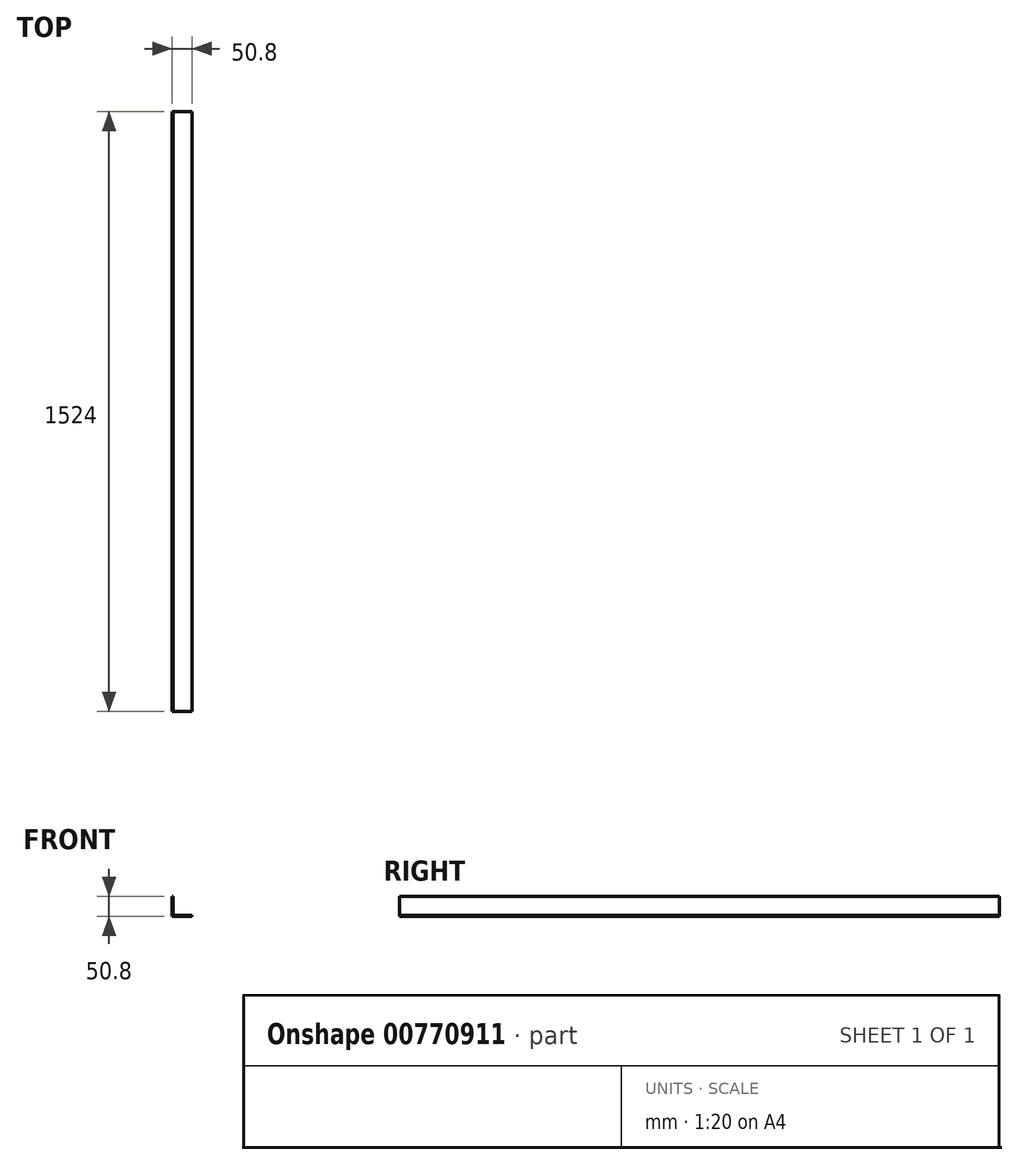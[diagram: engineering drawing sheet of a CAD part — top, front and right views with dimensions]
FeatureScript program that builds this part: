
annotation { "Feature Type Name" : "Feature", "Feature Type Description" : "" }
export const myFeature = defineFeature(function(context is Context, id is Id, definition is map)
    precondition{}
    {
        {
            var Q0;
            Q0=qCreatedBy(makeId("Front.planeOp"),FACE);
            var sketch = newSketch(context, id + "F0", { "sketchPlane" : qUnion([Q0])});
            skLineSegment(sketch, "E0.bottom", {"start": v(0, 0) * mm, "end": v(50.8, 0) * mm});
            skLineSegment(sketch, "E0.top", {"start": v(0, 3.18) * mm, "end": v(50.8, 3.18) * mm});
            skLineSegment(sketch, "E0.left", {"start": v(0, 0) * mm, "end": v(0, 3.18) * mm});
            skLineSegment(sketch, "E0.right", {"start": v(50.8, 0) * mm, "end": v(50.8, 3.18) * mm});
            skLineSegment(sketch, "E1.bottom", {"start": v(0, 0) * mm, "end": v(3.18, 0) * mm});
            skLineSegment(sketch, "E1.top", {"start": v(0, 50.8) * mm, "end": v(3.17, 50.8) * mm});
            skLineSegment(sketch, "E1.left", {"start": v(0, 0) * mm, "end": v(0, 50.8) * mm});
            skLineSegment(sketch, "E1.right", {"start": v(3.18, 0) * mm, "end": v(3.17, 50.8) * mm});
            skSolve(sketch);
        }
        {
            var Q0;
            Q0=qSketchRegion(id+"F0",true);
            extrude(context, id + "F1", {"entities" : qUnion([Q0]), "oppositeDirection" : true, "depth" : 1524 * mm, "offsetDistance" : 25.4 * mm});
        }
    });
